# Revit family: Sanitary_Other_hansgrohe_53002000-hansgrohe-Pipe-trap-standard-mo_
name_source: partatom
category: Plumbing Fixtures
revit_build: Autodesk Revit 2015 (Build: 20140903_1530(x64)
units: mm (PartAtom-declared; Revit-internal decimal feet)

## types (1)
- Chrome 000
    BIMobject category = Other
    BIMobject category code = sanitary-sanitary-other
    BIMobject main category = Sanitary
    BIMobject main category code = sanitary
    BOSUseNativeGeometries = 1
    Brand url = http://www.hansgrohe-int.com
    Default Elevation = 4' - 0"
    EAN code = https://4011097123912
    Edition number = 1
    IFC Classification = Furnishing Element
    Installation instructions = https://pro.hansgrohe-int.com
    Manufacturer country = Germany
    Manufacturer name = hansgrohe
    Material main = Chrome
    Material secondary = Chrome
    Product Guid = 973db18a-b868-4a57-9c98-ecf661d0ddc2
    Product SKU = 53002000
    Product data url = https://bimobject.com
    Product family = hansgrohe
    Product group = Siphons/Angle valves
    Product name = 53002000 hansgrohe Pipe trap standard model 53002000
    Product url = https://pro.hansgrohe-int.com
    QR code = http://bimobject.com
    Technical description = https://pro.hansgrohe-int.com
    UNSPSC Code = 401425
    Uniclass 1.4 Code = L824
    Uniclass 1.4 Description = Bathroom, toilet furniture and fittings

## geometry (parser evidence)
native form markers: Sweep x3
no freeform markers — native parametric forms only
